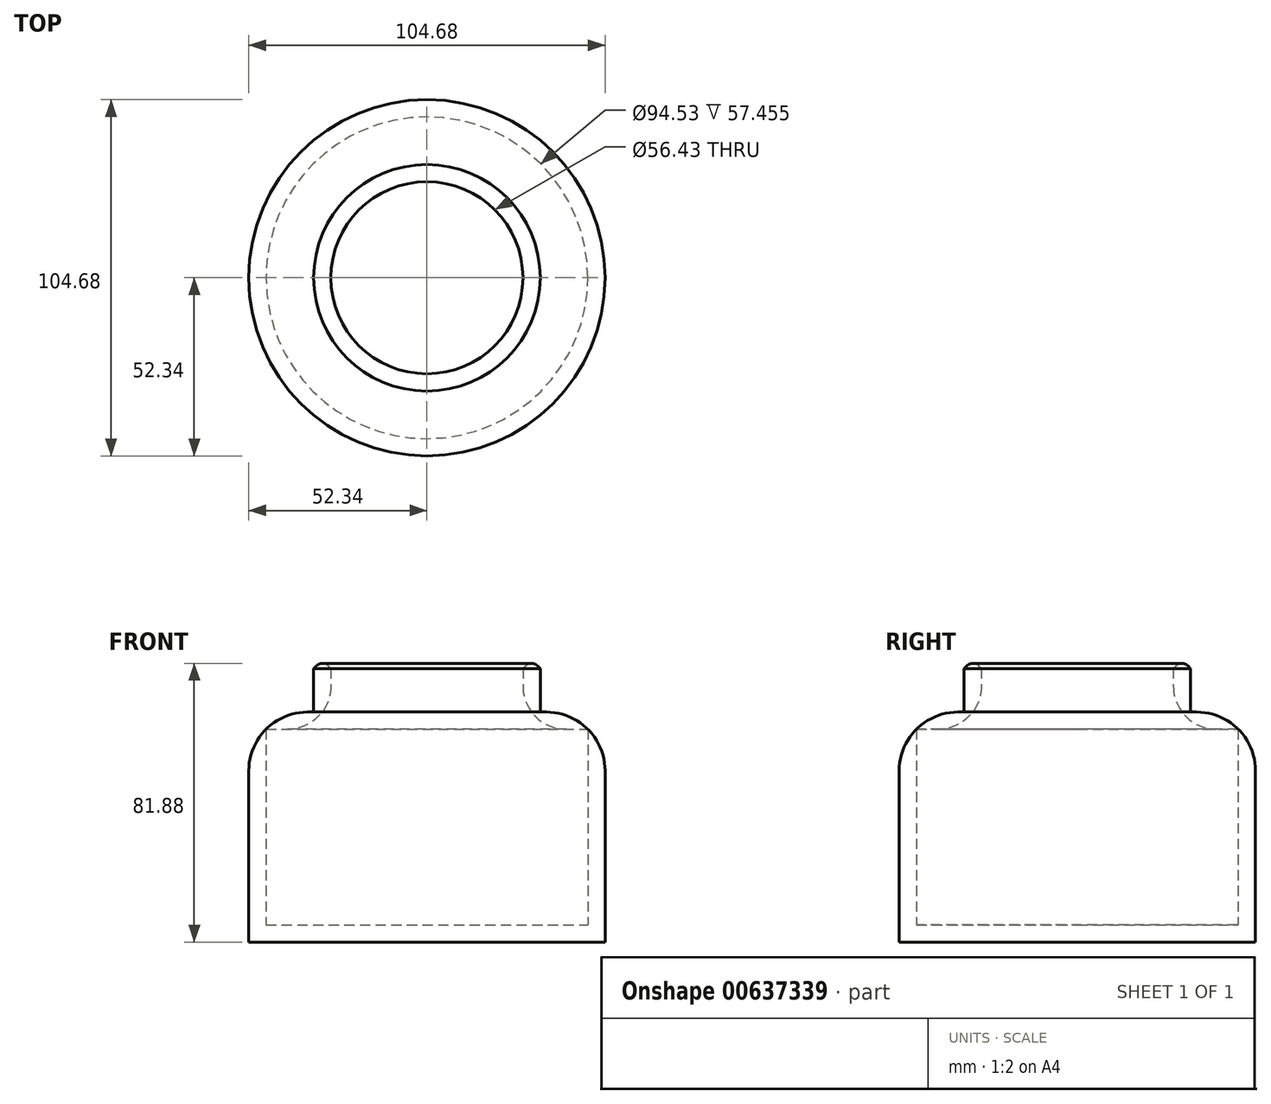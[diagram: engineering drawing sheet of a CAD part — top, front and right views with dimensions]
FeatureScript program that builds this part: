
annotation { "Feature Type Name" : "Feature", "Feature Type Description" : "" }
export const myFeature = defineFeature(function(context is Context, id is Id, definition is map)
    precondition{}
    {
        {
            var Q0;
            Q0=qCreatedBy(makeId("Front.planeOp"),FACE);
            var sketch = newSketch(context, id + "F0", { "sketchPlane" : qUnion([Q0])});
            skLineSegment(sketch, "E0", {"start": v(0, 0) * mm, "end": v(0, 76.8) * mm});
            skLineSegment(sketch, "E1", {"start": v(0, 76.8) * mm, "end": v(33.3, 76.8) * mm});
            skLineSegment(sketch, "E2", {"start": v(33.3, 76.8) * mm, "end": v(33.3, 67.6) * mm});
            skLineSegment(sketch, "E3", {"start": v(33.3, 67.6) * mm, "end": v(52.34, 67.6) * mm});
            skLineSegment(sketch, "E4", {"start": v(52.34, 67.6) * mm, "end": v(52.34, 0) * mm});
            skLineSegment(sketch, "E5", {"start": v(52.34, 0) * mm, "end": v(47.26, 0) * mm});
            skLineSegment(sketch, "E6", {"start": v(47.26, 62.53) * mm, "end": v(28.21, 62.53) * mm});
            skLineSegment(sketch, "E7", {"start": v(47.26, 5.08) * mm, "end": v(0, 5.08) * mm});
            skLineSegment(sketch, "E8", {"start": v(0, 5.08) * mm, "end": v(0, 0) * mm});
            skLineSegment(sketch, "E9", {"start": v(47.26, 0) * mm, "end": v(0, 0) * mm});
            skLineSegment(sketch, "E10", {"start": v(47.26, 62.53) * mm, "end": v(47.26, 5.08) * mm});
            skLineSegment(sketch, "E11", {"start": v(28.21, 62.53) * mm, "end": v(28.21, 76.8) * mm});
            skSolve(sketch);
        }
        {
            var Q0;
            {var subQ0=sQuery(id+"F0.wireOp",EDGE,"E2");Q0=makeQuery(id+"F0.imprint","IMPRINT",FACE,{"disambiguationData":[TD([[makeQuery(id+"F0.imprint","IMPRINT",EDGE,{"derivedFrom":subQ0}),-1.0]])]});}
            var Q1;
            Q1=sQuery(id+"F0.wireOp",EDGE,"E0");
            revolve(context, id + "F1", {"entities" : qUnion([Q0]), "axis" : qUnion([Q1]), "revolveType" : RevolveType.FULL});
        }
        {
            var Q0;
            Q0=makeQuery(id+"F1.opRevolve","SWEPT_EDGE",EDGE,{"disambiguationData":[OSD([sQuery(id+"F0.wireOp",EDGE,"E3"),sQuery(id+"F0.wireOp",EDGE,"E4")])]});
            fillet(context, id + "F2", {"entities" : qUnion([Q0]), "radius" : 17.27 * mm, "tangentPropagation" : true, "allowEdgeOverflow" : false});
        }
        {
            var Q0;
            Q0=makeQuery(id+"F1.opRevolve","SWEPT_FACE",FACE,{"disambiguationData":[OSD([sQuery(id+"F0.wireOp",EDGE,"E1")])]});
            extrude(context, id + "F3", {"entities" : qUnion([Q0]), "operationType" : NewBodyOperationType.ADD, "depth" : 5.08 * mm, "offsetDistance" : 25.4 * mm});
        }
        {
            var Q0;
            Q0=makeQuery(id+"F3.opExtrude","CAP_EDGE",EDGE,{"disambiguationData":[OSD([sQuery(id+"F0.wireOp",EDGE,"E1"),sQuery(id+"F0.wireOp",EDGE,"E11")])],"isStart":false});
            var Q1;
            Q1=makeQuery(id+"F3.opExtrude","CAP_EDGE",EDGE,{"disambiguationData":[OSD([sQuery(id+"F0.wireOp",EDGE,"E1"),sQuery(id+"F0.wireOp",EDGE,"E2")])],"isStart":false});
            chamfer(context, id + "F4", {"entities" : qUnion([Q0, Q1]), "width" : 1.52 * mm, "tangentPropagation" : true});
        }
        {
            var Q0;
            {var subQ0=sQuery(id+"F0.wireOp",EDGE,"E1");Q0=makeQuery(id+"F4.opChamfer","BLEND_EDGE",EDGE,{"blendedFrom":[makeQuery(id+"F3.opExtrude","CAP_EDGE",EDGE,{"disambiguationData":[OSD([subQ0,sQuery(id+"F0.wireOp",EDGE,"E2")])],"isStart":false}),makeQuery(id+"F3.opExtrude","CAP_FACE",FACE,{"disambiguationData":[OSD([subQ0])],"isStart":false})],"blendedInto":[makeQuery(id+"F3.opExtrude","CAP_FACE",FACE,{"disambiguationData":[OSD([subQ0])],"isStart":false})]});}
            var Q1;
            {var subQ0=sQuery(id+"F0.wireOp",EDGE,"E1");Q1=makeQuery(id+"F4.opChamfer","BLEND_EDGE",EDGE,{"blendedFrom":[makeQuery(id+"F3.opExtrude","CAP_EDGE",EDGE,{"disambiguationData":[OSD([subQ0,sQuery(id+"F0.wireOp",EDGE,"E11")])],"isStart":false}),makeQuery(id+"F3.opExtrude","CAP_FACE",FACE,{"disambiguationData":[OSD([subQ0])],"isStart":false})],"blendedInto":[makeQuery(id+"F3.opExtrude","CAP_FACE",FACE,{"disambiguationData":[OSD([subQ0])],"isStart":false})]});}
            fillet(context, id + "F5", {"entities" : qUnion([Q0, Q1]), "radius" : 2.41 * mm, "tangentPropagation" : true, "allowEdgeOverflow" : false});
        }
        {
            var Q0;
            Q0=makeQuery(id+"F1.opRevolve","SWEPT_EDGE",EDGE,{"disambiguationData":[OSD([sQuery(id+"F0.wireOp",EDGE,"E6"),sQuery(id+"F0.wireOp",EDGE,"E11")])]});
            fillet(context, id + "F6", {"entities" : qUnion([Q0]), "radius" : 12.7 * mm, "tangentPropagation" : true, "allowEdgeOverflow" : false});
        }
    });
